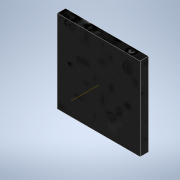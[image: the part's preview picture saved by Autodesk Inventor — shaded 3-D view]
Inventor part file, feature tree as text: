
AUTODESK INVENTOR PART (.ipt)
format: ipt  version: 2022 (Build 260153000, 153)  size: 114,176 bytes
history: native  units: mm
features: sketch x2, extrude x1, other x1, projected_geometry x1
ambient origin geometry x8: Origin, YZ Plane, XZ Plane, XY Plane, X Axis, Y Axis, Z Axis, Center Point
bodies: Solid1 (feature_tree)
feature tree (5):
  extrude  "Extrusion1"  Depth=31.75mm
  sketch  "Sketch2"  dims[d2=3.175mm d3=0.0mm]
  other  "Work Axis1"
  sketch  "Sketch1"  dims[d0=31.75mm d1=31.75mm]
  projected_geometry  "Projected Loop1"
